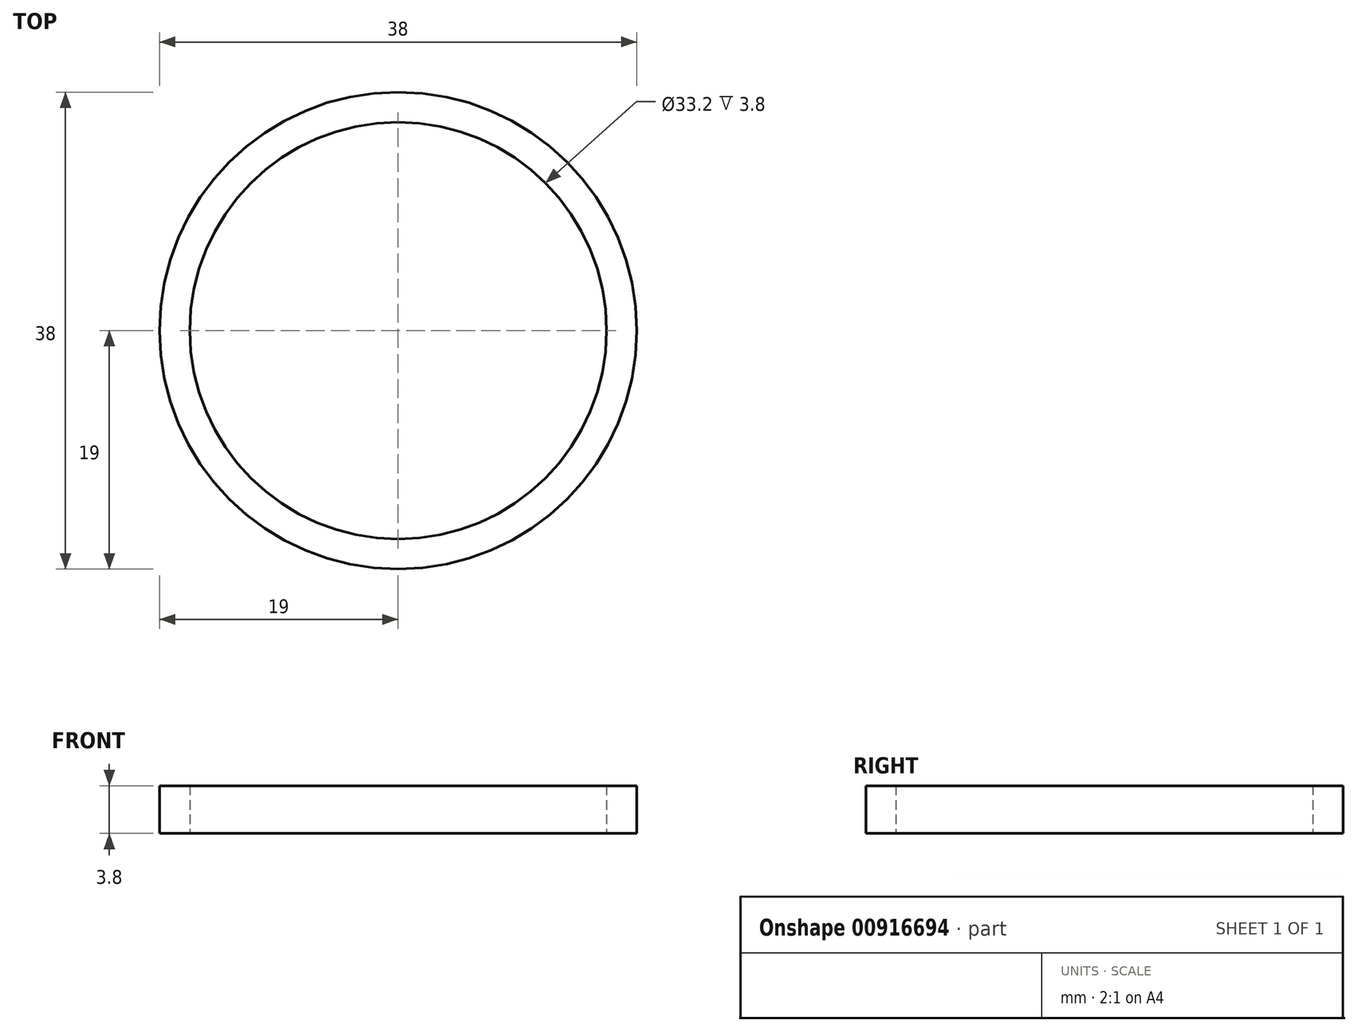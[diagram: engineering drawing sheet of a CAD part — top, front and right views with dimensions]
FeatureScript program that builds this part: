
annotation { "Feature Type Name" : "Feature", "Feature Type Description" : "" }
export const myFeature = defineFeature(function(context is Context, id is Id, definition is map)
    precondition{}
    {
        {
            var Q0;
            Q0=qCreatedBy(makeId("Top.planeOp"),FACE);
            var sketch = newSketch(context, id + "F0", { "sketchPlane" : qUnion([Q0])});
            skCircle(sketch, "E0", {"center": v(0, 0) * mm, "radius": 16.6 * mm});
            skCircle(sketch, "E1", {"center": v(0, 0) * mm, "radius": 19 * mm});
            skSolve(sketch);
        }
        {
            var Q0;
            Q0 = qSketchRegion(id + "F0", true);
            extrude(context, id + "F1", {"entities" : qUnion([Q0]), "depth" : 3.8 * mm, "offsetDistance" : 25 * mm});
        }
    });
